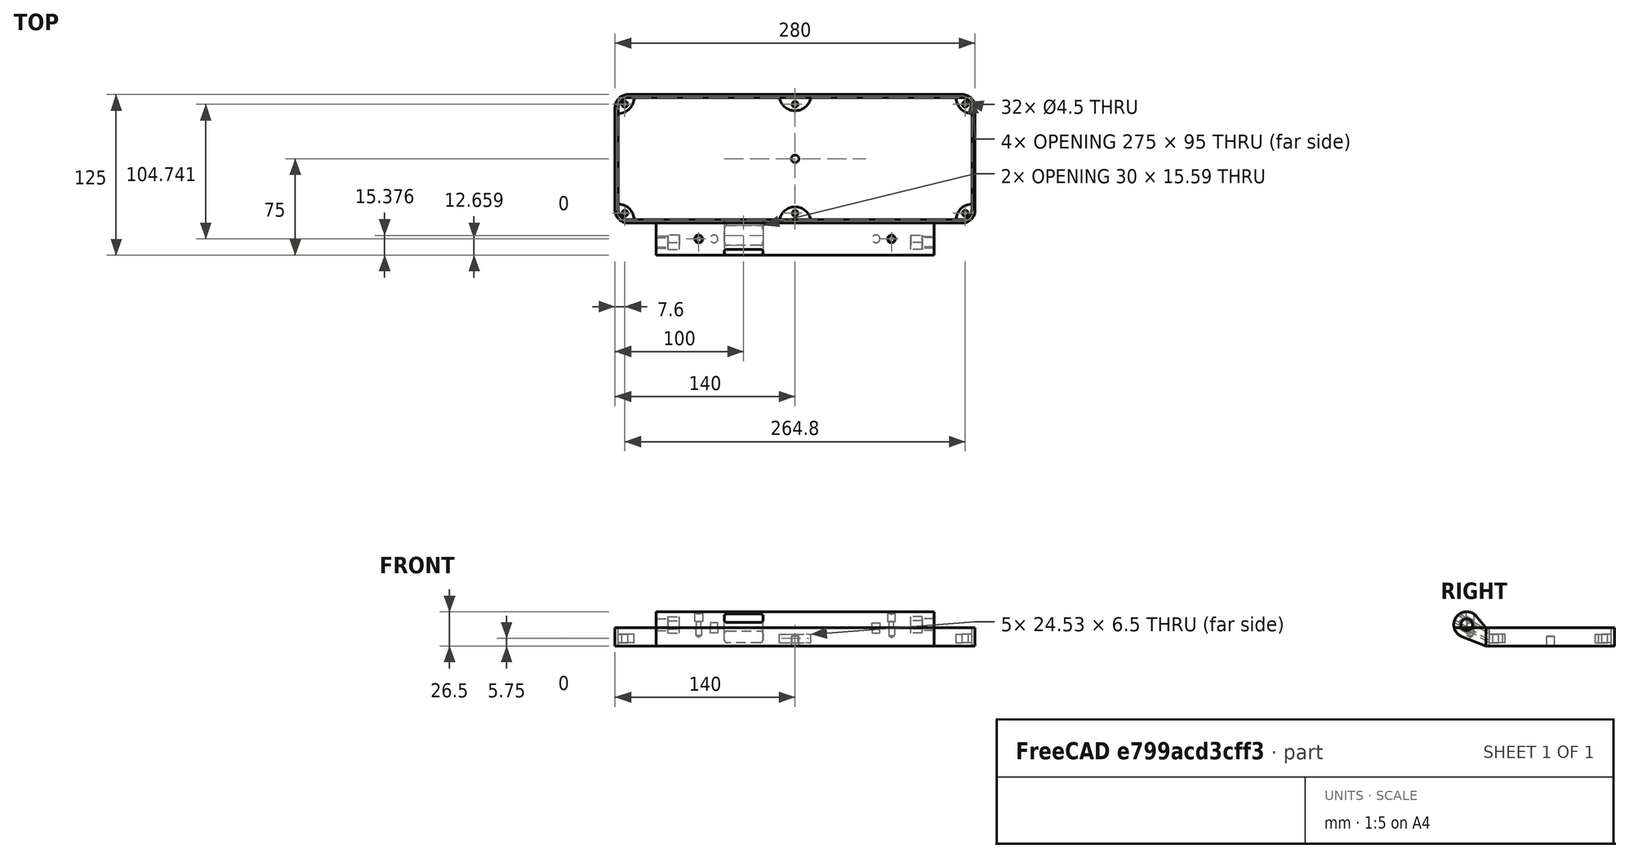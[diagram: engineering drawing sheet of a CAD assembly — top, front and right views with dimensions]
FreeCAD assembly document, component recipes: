
FREECAD ASSEMBLY — COMPONENT RECIPES ("TopEnclosureShell")

This assembly document has 7 components, labeled P0..P6 below (a component is one placed body or linked part). 7 of them carry a construction recipe — the FreeCAD feature program that regenerates the part from scratch, quoted from this document or its linked companion documents; the rest are supplied as boundary geometry only. No exploded tour is included for this assembly.
COMPONENT P0 — recipe-attached ("Top Enclosure Shell - Base", modeled in this document).
Construction recipe (the document's own serialized feature program — sketch geometry with constraints, then the solid features built on it; lengths are millimeters unless a unit is written):

FEATURE [PartDesign::SubShapeBinder] Binder
  BindCopyOnChange = 0
  BindMode = 0
  ClaimChildren = false
  Context = -> Body [Binder.]
  Fuse = false
  MakeFace = true
  OffsetFill = false
  OffsetIntersection = false
  OffsetJoinType = 0
  OffsetOpenResult = false
  PartialLoad = false
  Refine = true
  Relative = true
  Support = -> [Link001[Edge17,Edge1,Edge2,Edge18,Edge3,Edge19,Edge20,Edge4]]
  _Version = 2
FEATURE [PartDesign::Pad] Pad
  Direction = (0,0,1)
  Length = 14
  Length2 = 10
  Profile = -> Binder
  Refine = true
  Suppressed = false
  Type = 0
  expr: Length = <<Vars>>.top_enclosure_depth
FEATURE [PartDesign::SubShapeBinder] Binder001
  BindCopyOnChange = 0
  BindMode = 0
  ClaimChildren = false
  Context = -> Body [Binder001.]
  Fuse = false
  MakeFace = true
  OffsetFill = false
  OffsetIntersection = false
  OffsetJoinType = 0
  OffsetOpenResult = false
  PartialLoad = false
  Refine = true
  Relative = true
  Support = -> [Link001[Edge37,Edge39]]
  _Version = 2
FEATURE [Sketcher::SketchObject] Sketch
  ArcFitTolerance = 1e-06
  AttachmentOffset = pos=(0,0,2.5) rot=(0,0,1;0rad)
  AttachmentSupport = -> [XY_Plane]
  ExternalGeometry = -> [Binder001]
  FullyConstrained = true
  MakeInternals = false
  MapMode = 5
  Placement = pos=(0,0,2.5) rot=(0,0,1;0rad)
  expr: .AttachmentOffset.Base.z = <<LocalVars>>.bottom_offset
  sketch-geometry (4):
    g0: ArcOfCircle CenterX=-137.703 CenterY=47.7033 CenterZ=0 NormalX=0 NormalY=0 NormalZ=1 AngleXU=0 Radius=12.5 StartAngle=4.72865 EndAngle=6.26692
    g1: LineSegment StartX=-137.5 StartY=35.205 StartZ=0 EndX=-137.5 EndY=41.4 EndZ=0
    g2: LineSegment StartX=-125.205 StartY=47.5 StartZ=0 EndX=-131.4 EndY=47.5 EndZ=0
    g3: ArcOfCircle CenterX=-131.4 CenterY=41.4 CenterZ=0 NormalX=0 NormalY=0 NormalZ=1 AngleXU=0 Radius=6.1 StartAngle=1.5708 EndAngle=3.14159
  constraints (10):
    c: Coincident(g0,g-4)
    c: PointOnObject(g0,g-4)
    c: Horizontal(g-3,g0)
    c: Vertical(g-3,g0)
    c: Coincident(g1,g0)
    c: Coincident(g1,g-3)
    c: Coincident(g2,g0)
    c: Coincident(g2,g-3)
    c: Coincident(g3,g1)
    c: Tangent(g3,g2) = -1.5708
FEATURE [PartDesign::SubShapeBinder] Binder002
  BindCopyOnChange = 0
  BindMode = 0
  ClaimChildren = false
  Context = -> Body [Binder002.]
  Fuse = false
  MakeFace = true
  OffsetFill = false
  OffsetIntersection = false
  OffsetJoinType = 0
  OffsetOpenResult = false
  PartialLoad = false
  Refine = true
  Relative = true
  Support = -> [Link001[Edge38,Edge40]]
  _Version = 2
FEATURE [PartDesign::Pad] Pad001
  BaseFeature = -> Pad
  Direction = (0,0,1)
  Length = 6.5
  Length2 = 10
  Profile = -> Sketch
  ReferenceAxis = -> Sketch [N_Axis]
  Refine = true
  Suppressed = false
  Type = 0
  expr: Length = <<LocalVars>>.internal_depth
FEATURE [PartDesign::SubShapeBinder] Binder003
  BindCopyOnChange = 0
  BindMode = 0
  ClaimChildren = false
  Context = -> Body [Binder003.]
  Fuse = false
  MakeFace = true
  OffsetFill = false
  OffsetIntersection = false
  OffsetJoinType = 0
  OffsetOpenResult = false
  PartialLoad = false
  Refine = true
  Relative = true
  Support = -> [Binder001[Edge2]]
  _Version = 2
FEATURE [PartDesign::Hole] Hole
  BaseFeature = -> Pad001
  CustomThreadClearance = 0
  Depth = 25
  DepthType = 0
  Diameter = 4.5
  DrillForDepth = false
  DrillPoint = 1
  DrillPointAngle = 118
  HoleCutCountersinkAngle = 90
  HoleCutCustomValues = false
  HoleCutDepth = 0
  HoleCutDiameter = 6.1
  HoleCutType = 0
  ModelThread = false
  Profile = -> Binder003
  Refine = true
  Reversed = true
  Suppressed = false
  Tapered = false
  TaperedAngle = 90
  ThreadClass = 0
  ThreadDepth = 25
  ThreadDepthType = 0
  ThreadDirection = 0
  ThreadFit = 0
  ThreadSize = 0
  ThreadType = 0
  Threaded = false
  UseCustomThreadClearance = false
  expr: Diameter = <<Vars>>.nut_inserts_m3
FEATURE [PartDesign::Mirrored] Mirrored
  MirrorPlane = -> YZ_Plane
  Refine = true
  Suppressed = false
  TransformMode = 0
FEATURE [PartDesign::Mirrored] Mirrored001
  MirrorPlane = -> XZ_Plane
  Refine = true
  Suppressed = false
  TransformMode = 0
FEATURE [PartDesign::MultiTransform] MultiTransform
  BaseFeature = -> Hole
  Originals = -> [Pad001,Hole]
  Refine = true
  Suppressed = false
  TransformMode = 0
  Transformations = -> [Mirrored,Mirrored001]
FEATURE [Sketcher::SketchObject] Sketch001
  ArcFitTolerance = 1e-06
  AttachmentOffset = pos=(0,0,2.5) rot=(0,0,1;0rad)
  AttachmentSupport = -> [XY_Plane]
  ExternalGeometry = -> [Binder002]
  FullyConstrained = true
  MakeInternals = false
  MapMode = 5
  Placement = pos=(0,0,2.5) rot=(0,0,1;0rad)
  expr: .AttachmentOffset.Base.z = <<LocalVars>>.bottom_offset
  sketch-geometry (2):
    g0: ArcOfCircle CenterX=0 CenterY=49.9 CenterZ=0 NormalX=0 NormalY=0 NormalZ=1 AngleXU=0 Radius=12.5 StartAngle=3.33479 EndAngle=6.08999
    g1: LineSegment StartX=-12.2674 StartY=47.5 StartZ=0 EndX=12.2674 EndY=47.5 EndZ=0
  constraints (6):
    c: Coincident(g0,g-3)
    c: PointOnObject(g0,g-3)
    c: Horizontal(g1)
    c: PointOnObject(g1,g-4)
    c: Coincident(g1,g0)
    c: Coincident(g1,g0)
FEATURE [PartDesign::Pad] Pad002
  BaseFeature = -> MultiTransform
  Direction = (0,0,1)
  Length = 6.5
  Length2 = 10
  Profile = -> Sketch001
  ReferenceAxis = -> Sketch001 [N_Axis]
  Refine = true
  Suppressed = false
  Type = 0
  expr: Length = <<LocalVars>>.internal_depth
FEATURE [PartDesign::SubShapeBinder] Binder004
  BindCopyOnChange = 0
  BindMode = 0
  ClaimChildren = false
  Context = -> Body [Binder004.]
  Fuse = false
  MakeFace = true
  OffsetFill = false
  OffsetIntersection = false
  OffsetJoinType = 0
  OffsetOpenResult = false
  PartialLoad = false
  Refine = true
  Relative = true
  Support = -> [Binder002[Edge2]]
  _Version = 2
FEATURE [PartDesign::Hole] Hole001
  BaseFeature = -> Pad002
  CustomThreadClearance = 0
  Depth = 25
  DepthType = 0
  Diameter = 4.5
  DrillForDepth = false
  DrillPoint = 1
  DrillPointAngle = 118
  HoleCutCountersinkAngle = 90
  HoleCutCustomValues = false
  HoleCutDepth = 0
  HoleCutDiameter = 6.1
  HoleCutType = 0
  ModelThread = false
  Profile = -> Binder004
  Refine = true
  Reversed = true
  Suppressed = false
  Tapered = false
  TaperedAngle = 90
  ThreadClass = 0
  ThreadDepth = 25
  ThreadDepthType = 0
  ThreadDirection = 0
  ThreadFit = 0
  ThreadSize = 0
  ThreadType = 0
  Threaded = false
  UseCustomThreadClearance = false
  expr: Diameter = <<Vars>>.nut_inserts_m3
FEATURE [PartDesign::Mirrored] Mirrored002
  BaseFeature = -> Hole001
  MirrorPlane = -> XZ_Plane
  Originals = -> [Pad002,Hole001]
  Refine = true
  Suppressed = false
  TransformMode = 0
FEATURE [PartDesign::Body] Body  label="Top Enclosure Shell - Base"
  AllowCompound = false
  Group = -> [Binder,Pad,Sketch,Binder001,Binder002,Pad001,Binder003,Hole,MultiTransform,Mirrored,Mirrored001,Sketch001,Pad002,Binder004,Hole001,Mirrored002]
  Origin = -> Origin
  Tip = -> Mirrored002
COMPONENT P1 — recipe-attached ("Top Enclosure Shell - 1", modeled in this document).
Construction recipe (the document's own serialized feature program — sketch geometry with constraints, then the solid features built on it; lengths are millimeters unless a unit is written):

FEATURE [PartDesign::Boolean] Boolean
  Group = -> [Binder005]
  Refine = true
  Suppressed = false
  Type = 0
  UsePlacement = true
FEATURE [Sketcher::SketchObject] Sketch002
  ArcFitTolerance = 1e-06
  AttachmentSupport = -> [YZ_Plane001]
  FullyConstrained = true
  MakeInternals = false
  MapMode = 5
  Placement = pos=(0,0,0) rot=(0.57735,0.57735,0.57735;2.0944rad)
  expr: Constraints[2] = <<Vars>>.top_enclosure_height / 2
  expr: Constraints[3] = <<Vars>>.top_enclosure_depth
  sketch-geometry (12):
    g0: LineSegment StartX=-50 StartY=0 StartZ=0 EndX=-50 EndY=14 EndZ=0
    g1: LineSegment StartX=-50 StartY=14 StartZ=0 EndX=-57.275 EndY=22.8501 EndZ=0
    g2: LineSegment StartX=-50 StartY=0 StartZ=0 EndX=-68.5971 EndY=7.16934 EndZ=0
    g3: Circle CenterX=-65 CenterY=16.5 CenterZ=0 NormalX=0 NormalY=0 NormalZ=1 AngleXU=0 Radius=4.5
    g4: ArcOfCircle CenterX=-65 CenterY=16.5 CenterZ=0 NormalX=0 NormalY=0 NormalZ=1 AngleXU=0 Radius=10 StartAngle=0.688024 EndAngle=4.34444
    g5: LineSegment StartX=-65 StartY=22.85 StartZ=0 EndX=-70.4993 EndY=19.675 EndZ=0
    g6: LineSegment StartX=-70.4993 StartY=19.675 StartZ=0 EndX=-70.4993 EndY=13.325 EndZ=0
    g7: LineSegment StartX=-70.4993 StartY=13.325 StartZ=0 EndX=-65 EndY=10.15 EndZ=0
    g8: LineSegment StartX=-65 StartY=10.15 StartZ=0 EndX=-59.5007 EndY=13.325 EndZ=0
    g9: LineSegment StartX=-59.5007 StartY=13.325 StartZ=0 EndX=-59.5007 EndY=19.675 EndZ=0
    g10: LineSegment StartX=-59.5007 StartY=19.675 StartZ=0 EndX=-65 EndY=22.85 EndZ=0
    g11: Circle [constr] CenterX=-65 CenterY=16.5 CenterZ=0 NormalX=0 NormalY=0 NormalZ=1 AngleXU=0 Radius=6.35
  constraints (29):
    c: PointOnObject(g0,g-1)
    c: Vertical(g0)
    c: DistanceX(g0,g-1) = 50
    c: DistanceY(g0,g0) = 14
    c: Coincident(g1,g0)
    c: Coincident(g2,g0)
    c: Coincident(g4,g3)
    c: Tangent(g1,g4) = -1.5708
    c: Tangent(g2,g4) = 1.5708
    c: Diameter(g4) = 20
    c: DistanceX(g3,g0) = 15
    c: DistanceY(g0,g3) = 2.5
    c: Diameter(g3) = 9
    c: Coincident(g5,g6)
    c: Coincident(g6,g7)
    c: Coincident(g7,g8)
    c: Coincident(g8,g9)
    c: Coincident(g9,g10)
    c: Coincident(g10,g5)
    c: Equal(g5, g6-g10) x5
    c: PointOnObject(g5,g11)
    c: PointOnObject(g6,g11)
    c: PointOnObject(g7,g11)
    c: PointOnObject(g8,g11)
    c: PointOnObject(g9,g11)
    c: PointOnObject(g10,g11)
    c: Coincident(g11,g3)
    c: Vertical(g5,g3)
    c: DistanceY(g6,g6) = 6.35
FEATURE [PartDesign::SubShapeBinder] Binder006
  BindCopyOnChange = 0
  BindMode = 0
  ClaimChildren = false
  Context = -> Body001 [Binder006.]
  Fuse = false
  MakeFace = true
  OffsetFill = false
  OffsetIntersection = false
  OffsetJoinType = 0
  OffsetOpenResult = false
  PartialLoad = false
  Refine = true
  Relative = true
  Support = -> [Sketch002[Edge2,Edge3,Edge4,Edge1]]
  _Version = 2
FEATURE [PartDesign::Pad] Pad003
  BaseFeature = -> Boolean
  Direction = (1,0,0)
  Length = 216
  Length2 = 10
  Midplane = true
  Profile = -> Binder006
  Refine = true
  Suppressed = false
  Type = 0
  expr: Length = <<Vars>>.top_enclosure_width - 32 * 2
FEATURE [PartDesign::SubShapeBinder] Binder007
  BindCopyOnChange = 0
  BindMode = 0
  ClaimChildren = false
  Context = -> Body001 [Binder007.]
  Fuse = false
  MakeFace = true
  OffsetFill = false
  OffsetIntersection = false
  OffsetJoinType = 0
  OffsetOpenResult = false
  PartialLoad = false
  Placement = pos=(99,0,0) rot=(0,0,1;0rad)
  Refine = true
  Relative = true
  Support = -> [Sketch002[Edge5]]
  _Version = 2
  expr: .Placement.Base.x = <<Vars>>.top_enclosure_width / 2 - 32 - 9
FEATURE [PartDesign::SubShapeBinder] Binder008
  BindCopyOnChange = 0
  BindMode = 0
  ClaimChildren = false
  Context = -> Body001 [Binder008.]
  Fuse = false
  MakeFace = true
  OffsetFill = false
  OffsetIntersection = false
  OffsetJoinType = 0
  OffsetOpenResult = false
  PartialLoad = false
  Placement = pos=(99,0,0) rot=(0,0,1;0rad)
  Refine = true
  Relative = true
  Support = -> [Sketch002[Edge6,Edge11,Edge10,Edge9,Edge8,Edge7]]
  _Version = 2
  expr: .Placement.Base.x = <<Vars>>.top_enclosure_width / 2 - 32 - 9
FEATURE [PartDesign::Pocket] Pocket
  BaseFeature = -> Pad003
  Direction = (-1,0,0)
  Length = 5
  Length2 = 5
  Profile = -> Binder007
  Refine = true
  Reversed = true
  Suppressed = false
  Type = 1
FEATURE [PartDesign::Pocket] Pocket001
  BaseFeature = -> Pocket
  Direction = (-1,0,0)
  Length = 9
  Length2 = 5
  Profile = -> Binder008
  Refine = true
  Suppressed = false
  Type = 0
FEATURE [PartDesign::Mirrored] Mirrored003
  BaseFeature = -> Pocket001
  MirrorPlane = -> YZ_Plane001
  Originals = -> [Pocket,Pocket001]
  Refine = true
  Suppressed = false
  TransformMode = 0
FEATURE [PartDesign::Body] Body001  label="Top Enclosure Shell - 1"
  AllowCompound = false
  Group = -> [Boolean,Sketch002,Binder006,Pad003,Binder007,Binder008,Pocket,Pocket001,Mirrored003]
  Origin = -> Origin001
  Tip = -> Mirrored003
COMPONENT P2 — recipe-attached ("Top Enclosure Shell - 2", modeled in this document).
Construction recipe (the document's own serialized feature program — sketch geometry with constraints, then the solid features built on it; lengths are millimeters unless a unit is written):

FEATURE [PartDesign::Boolean] Boolean001
  Group = -> [Binder009]
  Refine = true
  Suppressed = false
  Type = 0
  UsePlacement = true
FEATURE [Sketcher::SketchObject] Sketch003
  ArcFitTolerance = 1e-06
  AttachmentSupport = -> [Boolean001]
  ExternalGeometry = -> [Boolean001]
  FullyConstrained = false
  MakeInternals = false
  MapMode = 5
  Placement = pos=(0,-47.5,0) rot=(0,0.707107,0.707107;3.14159rad)
  expr: Constraints[26] = <<Vars>>.wire_hole_offset_x
  expr: Constraints[28] = <<Vars>>.wire_hole_height
  expr: Constraints[4] = <<Vars>>.wire_hole_width
  sketch-geometry (13):
    g0: LineSegment StartX=25 StartY=9.5 StartZ=0 EndX=25 EndY=4.5 EndZ=0
    g1: LineSegment StartX=27 StartY=2.5 StartZ=0 EndX=53 EndY=2.5 EndZ=0
    g2: LineSegment StartX=55 StartY=4.5 StartZ=0 EndX=55 EndY=9.5 EndZ=0
    g3: LineSegment StartX=53 StartY=11.5 StartZ=0 EndX=27 EndY=11.5 EndZ=0
    g4: ArcOfCircle CenterX=27 CenterY=9.5 CenterZ=0 NormalX=0 NormalY=0 NormalZ=1 AngleXU=0 Radius=2 StartAngle=1.5708 EndAngle=3.14159
    g5: GeomPoint [constr] X=25 Y=11.5 Z=0
    g6: ArcOfCircle CenterX=27 CenterY=4.5 CenterZ=0 NormalX=0 NormalY=0 NormalZ=1 AngleXU=0 Radius=2 StartAngle=3.14159 EndAngle=4.71239
    g7: GeomPoint [constr] X=25 Y=2.5 Z=0
    g8: ArcOfCircle CenterX=53 CenterY=4.5 CenterZ=0 NormalX=0 NormalY=0 NormalZ=1 AngleXU=0 Radius=2 StartAngle=4.71239 EndAngle=6.28319
    g9: GeomPoint [constr] X=55 Y=2.5 Z=0
    g10: ArcOfCircle CenterX=53 CenterY=9.5 CenterZ=0 NormalX=0 NormalY=0 NormalZ=1 AngleXU=0 Radius=2 StartAngle=0 EndAngle=1.5708
    g11: GeomPoint [constr] X=55 Y=11.5 Z=0
    g12: GeomPoint X=40 Y=7 Z=0
  constraints (29):
    c: Vertical(g0)
    c: Vertical(g2)
    c: Horizontal(g1)
    c: Horizontal(g3)
    c: DistanceX(g5,g11) = 30
    c: PointOnObject(g5,g0)
    c: PointOnObject(g5,g3)
    c: Tangent(g0,g4) = -1.5708
    c: Tangent(g3,g4) = -1.5708
    c: PointOnObject(g7,g0)
    c: PointOnObject(g7,g1)
    c: Tangent(g0,g6) = -1.5708
    c: Tangent(g1,g6) = -1.5708
    c: PointOnObject(g9,g1)
    c: PointOnObject(g9,g2)
    c: Tangent(g1,g8) = -1.5708
    c: Tangent(g2,g8) = -1.5708
    c: PointOnObject(g11,g2)
    c: PointOnObject(g11,g3)
    c: Tangent(g2,g10) = -1.5708
    c: Tangent(g3,g10) = -1.5708
    c: Equal(g8,g10)
    c: Equal(g10,g4)
    c: Equal(g4,g6)
    c: Radius(g6) = 2
    c: Symmetric(g7,g11,g12)
    c: DistanceX(g-1,g12) = 40
    c: DistanceY(g-1,g12) = 7
    c: DistanceY(g1,g3) = 9
FEATURE [Sketcher::SketchObject] Sketch004
  ArcFitTolerance = 1e-06
  AttachmentSupport = -> [YZ_Plane002]
  ExternalGeometry = -> [Boolean001]
  FullyConstrained = true
  MakeInternals = false
  MapMode = 5
  Placement = pos=(0,0,0) rot=(0.57735,0.57735,0.57735;2.0944rad)
  sketch-geometry (1):
    g0: LineSegment StartX=-84.641 StartY=27 StartZ=0 EndX=-50 EndY=7 EndZ=0
  constraints (3):
    c: Symmetric(g-4,g-4,g0)
    c: Distance(g0) = 40
    c: Angle(g0,g-1) = 0.523599
FEATURE [PartDesign::Pocket] Pocket002
  BaseFeature = -> Boolean001
  Direction = (0,-0.866025,0.5)
  Length = 5
  Length2 = 5
  Profile = -> Sketch003
  ReferenceAxis = -> Sketch004 [Edge1]
  Refine = true
  Suppressed = false
  Type = 1
FEATURE [PartDesign::Body] Body002  label="Top Enclosure Shell - 2"
  AllowCompound = false
  Group = -> [Boolean001,Sketch003,Sketch004,Pocket002]
  Origin = -> Origin002
  Tip = -> Pocket002
COMPONENT P3 — recipe-attached ("Top Enclosure Shell Split", modeled in this document).
Construction recipe (the document's own serialized feature program — sketch geometry with constraints, then the solid features built on it; lengths are millimeters unless a unit is written):

FEATURE [PartDesign::Boolean] Boolean002
  Group = -> [Binder010]
  Refine = true
  Suppressed = false
  Type = 0
  UsePlacement = true
FEATURE [Sketcher::SketchObject] Sketch005
  ArcFitTolerance = 1e-06
  AttachmentSupport = -> [YZ_Plane003]
  FullyConstrained = true
  MakeInternals = false
  MapMode = 5
  Placement = pos=(0,0,0) rot=(0.57735,0.57735,0.57735;2.0944rad)
  expr: Constraints[1] = <<Vars>>.top_enclosure_depth
  expr: Constraints[2] = <<Vars>>.top_enclosure_height / 2 - 10
  sketch-geometry (1):
    g0: LineSegment StartX=-90 StartY=14 StartZ=0 EndX=-40 EndY=14 EndZ=0
  constraints (4):
    c: Horizontal(g0)
    c: DistanceY(g-1,g0) = 14
    c: DistanceX(g0,g-1) = 40
    c: DistanceX(g0,g0) = 50
FEATURE [PartDesign::Body] Body003  label="Top Enclosure Shell Split"
  AllowCompound = false
  Group = -> [Boolean002,Sketch005]
  Origin = -> Origin003
  Tip = -> Boolean002
COMPONENT P4 — recipe-attached ("Top Enclosure Shell Part 1", modeled in this document).
Construction recipe (the document's own serialized feature program — sketch geometry with constraints, then the solid features built on it; lengths are millimeters unless a unit is written):

FEATURE [PartDesign::Boolean] Boolean003
  Group = -> [Binder011]
  Refine = true
  Suppressed = false
  Type = 0
  UsePlacement = true
FEATURE [PartDesign::SubShapeBinder] Binder014
  BindCopyOnChange = 0
  BindMode = 0
  ClaimChildren = false
  Context = -> Body004 [Binder014.]
  Fuse = false
  MakeFace = true
  OffsetFill = false
  OffsetIntersection = false
  OffsetJoinType = 0
  OffsetOpenResult = false
  PartialLoad = false
  Refine = true
  Relative = true
  Support = -> [Body006[Sketch006.]]
  _Version = 2
FEATURE [PartDesign::Hole] Hole002
  BaseFeature = -> Boolean003
  CustomThreadClearance = 0
  Depth = 6
  DepthType = 0
  Diameter = 4.5
  DrillForDepth = false
  DrillPoint = 1
  DrillPointAngle = 118
  HoleCutCountersinkAngle = 90
  HoleCutCustomValues = false
  HoleCutDepth = 0
  HoleCutDiameter = 6.1
  HoleCutType = 0
  ModelThread = false
  Profile = -> Binder014
  Refine = true
  Suppressed = false
  Tapered = false
  TaperedAngle = 90
  ThreadClass = 0
  ThreadDepth = 6
  ThreadDepthType = 0
  ThreadDirection = 0
  ThreadFit = 0
  ThreadSize = 0
  ThreadType = 0
  Threaded = false
  UseCustomThreadClearance = false
  expr: Diameter = <<Vars>>.nut_inserts_m3
FEATURE [PartDesign::Mirrored] Mirrored004
  BaseFeature = -> Hole002
  MirrorPlane = -> YZ_Plane004
  Originals = -> [Hole002]
  Refine = true
  Suppressed = false
  TransformMode = 0
FEATURE [PartDesign::SubShapeBinder] Binder017
  BindCopyOnChange = 0
  BindMode = 0
  ClaimChildren = false
  Context = -> Body004 [Binder017.]
  Fuse = false
  MakeFace = true
  OffsetFill = false
  OffsetIntersection = false
  OffsetJoinType = 0
  OffsetOpenResult = false
  PartialLoad = false
  Refine = true
  Relative = true
  Support = -> [Body006[Sketch007.]]
  _Version = 2
FEATURE [PartDesign::Pocket] Pocket004
  BaseFeature = -> Mirrored004
  Direction = (0,0,-1)
  Length = 4
  Length2 = 5
  Profile = -> Binder017
  Refine = true
  Suppressed = false
  Type = 0
FEATURE [PartDesign::Mirrored] Mirrored006
  BaseFeature = -> Pocket004
  MirrorPlane = -> YZ_Plane004
  Originals = -> [Pocket004]
  Refine = true
  Suppressed = false
  TransformMode = 0
FEATURE [PartDesign::Body] Body004  label="Top Enclosure Shell Part 1"
  AllowCompound = false
  Group = -> [Boolean003,Binder014,Hole002,Mirrored004,Binder017,Pocket004,Mirrored006]
  Origin = -> Origin004
  Tip = -> Mirrored006
COMPONENT P5 — recipe-attached ("Top Enclosure Shell Part 2", modeled in this document).
Construction recipe (the document's own serialized feature program — sketch geometry with constraints, then the solid features built on it; lengths are millimeters unless a unit is written):

FEATURE [PartDesign::Boolean] Boolean004
  Group = -> [Binder012]
  Refine = true
  Suppressed = false
  Type = 0
  UsePlacement = true
FEATURE [PartDesign::SubShapeBinder] Binder015
  BindCopyOnChange = 0
  BindMode = 0
  ClaimChildren = false
  Context = -> Body005 [Binder015.]
  Fuse = false
  MakeFace = true
  OffsetFill = false
  OffsetIntersection = false
  OffsetJoinType = 0
  OffsetOpenResult = false
  PartialLoad = false
  Refine = true
  Relative = true
  Support = -> [Body006[Sketch006.]]
  _Version = 2
FEATURE [PartDesign::SubShapeBinder] Binder016
  BindCopyOnChange = 0
  BindMode = 0
  ClaimChildren = false
  Context = -> Body005 [Binder016.]
  Fuse = false
  MakeFace = true
  Offset = 1.5
  OffsetFill = false
  OffsetIntersection = false
  OffsetJoinType = 0
  OffsetOpenResult = false
  PartialLoad = false
  Placement = pos=(0,0,15) rot=(0,0,1;0rad)
  Refine = true
  Relative = true
  Support = -> [Body006[Sketch006.]]
  _Version = 2
FEATURE [PartDesign::Hole] Hole003
  BaseFeature = -> Boolean004
  CustomThreadClearance = 0
  Depth = 25
  DepthType = 0
  Diameter = 3.6
  DrillForDepth = false
  DrillPoint = 1
  DrillPointAngle = 118
  HoleCutCountersinkAngle = 90
  HoleCutCustomValues = false
  HoleCutDepth = 0
  HoleCutDiameter = 6.1
  HoleCutType = 0
  ModelThread = false
  Profile = -> Binder015
  Refine = true
  Reversed = true
  Suppressed = false
  Tapered = false
  TaperedAngle = 90
  ThreadClass = 0
  ThreadDepth = 25
  ThreadDepthType = 0
  ThreadDirection = 0
  ThreadFit = 2
  ThreadSize = 9
  ThreadType = 1
  Threaded = false
  UseCustomThreadClearance = false
FEATURE [PartDesign::Pocket] Pocket003
  BaseFeature = -> Hole003
  Direction = (0,0,-1)
  Length = 10
  Length2 = 5
  Offset = 2
  Profile = -> Binder016
  Refine = true
  Suppressed = false
  Type = 0
FEATURE [PartDesign::Mirrored] Mirrored005
  BaseFeature = -> Pocket003
  MirrorPlane = -> YZ_Plane005
  Originals = -> [Hole003,Pocket003]
  Refine = true
  Suppressed = false
  TransformMode = 0
FEATURE [PartDesign::SubShapeBinder] Binder018
  BindCopyOnChange = 0
  BindMode = 0
  ClaimChildren = false
  Context = -> Body005 [Binder018.]
  Fuse = false
  MakeFace = true
  OffsetFill = false
  OffsetIntersection = false
  OffsetJoinType = 0
  OffsetOpenResult = false
  PartialLoad = false
  Refine = true
  Relative = true
  Support = -> [Body006[Sketch007.]]
  _Version = 2
FEATURE [PartDesign::Pocket] Pocket005
  BaseFeature = -> Mirrored005
  Direction = (0,0,-1)
  Length = 4
  Length2 = 5
  Profile = -> Binder018
  Refine = true
  Reversed = true
  Suppressed = false
  Type = 0
FEATURE [PartDesign::Mirrored] Mirrored007
  BaseFeature = -> Pocket005
  MirrorPlane = -> YZ_Plane005
  Originals = -> [Pocket005]
  Refine = true
  Suppressed = false
  TransformMode = 0
FEATURE [PartDesign::Body] Body005  label="Top Enclosure Shell Part 2"
  AllowCompound = false
  Group = -> [Boolean004,Binder015,Binder016,Hole003,Pocket003,Mirrored005,Binder018,Pocket005,Mirrored007]
  Origin = -> Origin005
  Tip = -> Mirrored007
COMPONENT P6 — recipe-attached ("Parts Join Helper", modeled in this document).
Construction recipe (the document's own serialized feature program — sketch geometry with constraints, then the solid features built on it; lengths are millimeters unless a unit is written):

FEATURE [PartDesign::SubShapeBinder] Binder019
  BindCopyOnChange = 0
  BindMode = 0
  ClaimChildren = false
  Context = -> Body007 [Binder019.]
  Fuse = false
  MakeFace = true
  OffsetFill = false
  OffsetIntersection = false
  OffsetJoinType = 0
  OffsetOpenResult = false
  PartialLoad = false
  Refine = true
  Relative = true
  Support = -> [Body006[Sketch007.Edge1]]
  _Version = 2
FEATURE [Sketcher::SketchObject] Sketch008
  ArcFitTolerance = 1e-06
  AttachmentSupport = -> [XY_Plane007]
  ExternalGeometry = -> [Binder019]
  FullyConstrained = true
  MakeInternals = false
  MapMode = 5
  expr: Constraints[2] = 6 - <<Vars>>.clearance / 2
  sketch-geometry (1):
    g0: Circle CenterX=0 CenterY=0 CenterZ=0 NormalX=0 NormalY=0 NormalZ=1 AngleXU=0 Radius=2.95
  constraints (3):
    c: Coincident(g0,g-1)
    c: Diameter(g-3) = 6
    c: Diameter(g0) = 5.9
FEATURE [PartDesign::Pad] Pad004
  Direction = (0,0,1)
  Length = 7.6
  Length2 = 10
  Profile = -> Sketch008
  ReferenceAxis = -> Sketch008 [N_Axis]
  Refine = true
  Suppressed = false
  Type = 0
  expr: Length = 8 - 2 * <<Vars>>.clearance
FEATURE [PartDesign::Body] Body007  label="Parts Join Helper"
  AllowCompound = false
  Group = -> [Binder019,Sketch008,Pad004]
  Origin = -> Origin007
  Tip = -> Pad004
PROVENANCE & LICENSES
A FreeCAD (.FCStd) document from a public repository crawl; recipes are the document's own serialized feature recipes (and, for linked parts, companion documents' recipes).
License: as declared in the source repository (recorded in the dataset sidecar).
